# Revit family: conv_troax_wall_fencedoor_ur350
name_source: partatom
category: Sonderausstattung
revit_build: Autodesk Revit 2017 (Build: 20160225_1515(x64)
units: mm (PartAtom-declared; Revit-internal decimal feet)

## family parameters
Arbeitsebenenbasiert = Nein
Beim Laden mit Abzugskörper schneiden = Nein
Bemaßung runder Anschluss = Durchmesser verwenden
Gemeinsam genutzt = Nein
Immer vertikal = Ja
OmniClass-Nummer = 23.25.40.21.21.11
OmniClass-Titel = Swinging Gates
Raumberechnungspunkt = Nein
Teiletyp = Normal

## types (2) — shared parameters
AssetType = Fixed
Beschreibung = The UR 350 Padlock door is primarily designed to be used together with Troax UR 350 mesh panel. UR 350 doors and panels are ideal for secure environments where the risk of break-ins is low. The door leaf has a 30x20 mm steel tube frame and two horizontal tubes to create strength and stability. The 50x50 mesh aperture also makes it virtually impossible for a hand to reach through the mesh. Doors are supplied preassembled and are ready for installation.
Brand = Troax
Category = Doors
Color = Grey
Constituents = Cut profile: various length to use after cut height on site; End profile UR/UX L=2200 to use after cut panel length on site; U-profile UR 19x19x2200 various length to use after cut on site
DurationUnit = Year
Features = The door leaf has a 30x20 mm steel tube frame and two horizontal tubes to create strength and stability. The 50x50 mesh aperture also makes it virtually impossible for a hand to reach through the mesh. Doors are supplied preassembled and are ready for installation.
Finish = Powder coated as standard with a grey RAL 7037 finish. However other RAL colors are available upon request.
FurniturePanelType = Other
HasOpening = Ja
Hersteller = Troax
IfcExportAs = IfcSystemFurnitureElementTypePanel
IfcExportType = DOOR
MainColor = Grey
ManufacturerName = Troax
ManufacturerURL = https://www.troax.com
Material = Carbon steel
NBSDescription = Metal doorsets
NBSReference = 45-25-28/344
NominalDepth = 76 mm  [stored 0.249344 ft]
NominalHeight = 2200 mm
ProductDatasheet = https://www.troax.com
ProductInformation = Troax Classic is an excellent choice of mesh partition for storage spaces in apartment buildings, cellars and attics that already have exterior protection or where there is a low risk of tampering.
Shape = Sculptured
Uniclass2 = Pr_30_59_23_11
Uniclass2015Description = Carbon steel door frames
Uniclass2015Reference = Pr_30_59_23_11
Version = 1
VersionDate = 12/11/2018
WallPanelMainMaterial = Steel, Carbon
WarrantyDurationUnit = Year
zero-valued in all types: Kosten, NominalThickness

## per-type parameters (varying)
| type | ConvergoRefNr | DoorType | Name | NominalWidth | Size | URL |
| Troax classic UR 350 900mm | 0054-1811-0033-SE | Door ur350 900 | Wall_FenceDoor_UR350_900 | 918 mm  [stored 3.01181 ft] | 76x2200x918 mm | https://www.troax.com |
| Troax classic UR 350 750mm | 0054-1811-0032-SE | Door ur350 750 | Wall_FenceDoor_UR350_750 | 768 mm  [stored 2.51969 ft] | 76x2200x768 mm |  |

note: column(s) folded — value = type name in every type: Modell

note: [stored X ft] marks values corroborated as IEEE doubles in the binary element streams (Revit-internal decimal feet)

## geometry (parser evidence)
native form markers: Blend x4, Sweep x4
no freeform markers — native parametric forms only
